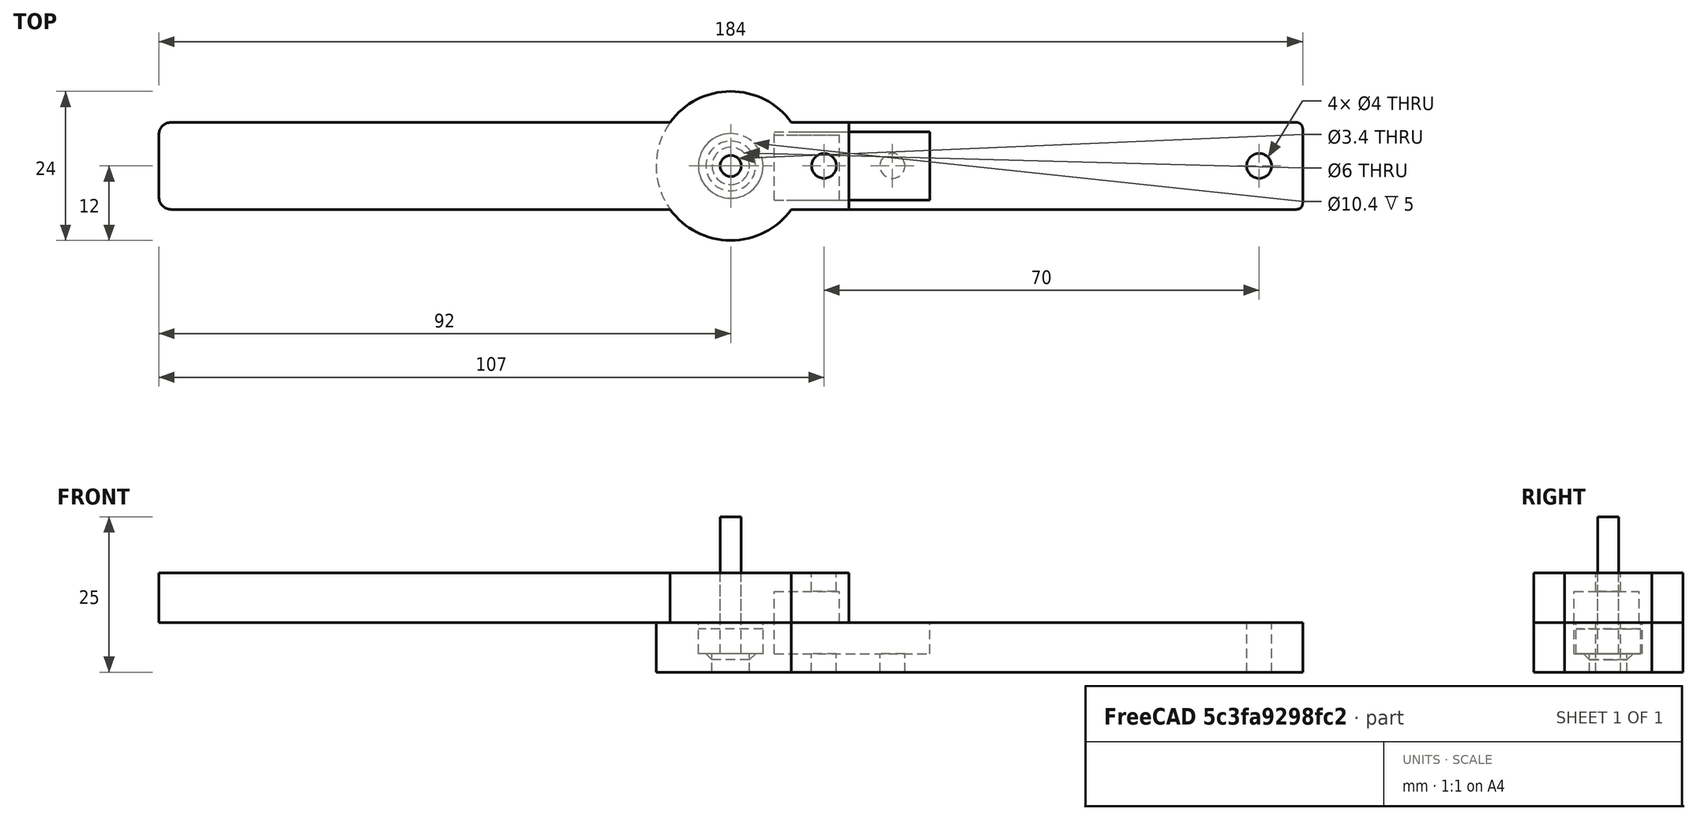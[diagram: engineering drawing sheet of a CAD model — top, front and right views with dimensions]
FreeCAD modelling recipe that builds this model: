
FCSTD DOCUMENT  (FreeCAD 0.17R13522 (Git))
Label: Magnet Testing parts
License: All rights reserved
LicenseURL: http://en.wikipedia.org/wiki/All_rights_reserved
objects: Part::Cylinder×14, Part::Cut×7, Part::Box×6, Part::Fuse×6, Part::Fillet×4, Part::Chamfer×1, Part::MultiFuse×1
note: 39 computed .brp shape members not serialized (recipe doc carries the construction recipe); baked Part::Feature solids carry a one-line shape summary decoded from their .brp

FEATURE [Part::Cylinder] Cylinder
  Angle = 360
  AttacherType = Attacher::AttachEngine3D
  Height = 8
  Radius = 12
FEATURE [Part::Box] Box  label="Long Magnet"
  AttacherType = Attacher::AttachEngine3D
  Height = 5
  Length = 25
  Placement = pos=(7,-5.5,3) rot=(0,0,1;0rad)
  Width = 11
FEATURE [Part::Cylinder] Cylinder001
  Angle = 360
  AttacherType = Attacher::AttachEngine3D
  Height = 25
  Radius = 1.7
FEATURE [Part::Cylinder] Cylinder002
  Angle = 360
  AttacherType = Attacher::AttachEngine3D
  Height = 3
  Radius = 3
FEATURE [Part::Cylinder] Cylinder003  label="bearing"
  Angle = 360
  AttacherType = Attacher::AttachEngine3D
  Height = 4
  Placement = pos=(0,0,3) rot=(0,0,1;0rad)
  Radius = 5.2
FEATURE [Part::Fuse] Fusion  label="Screw"
  Base = -> Cylinder001
  Tool = -> Cylinder002
FEATURE [Part::Cylinder] Cylinder004  label="bearing001"
  Angle = 360
  AttacherType = Attacher::AttachEngine3D
  Height = 5
  Placement = pos=(0,0,3) rot=(0,0,1;0rad)
  Radius = 5.2
FEATURE [Part::Cylinder] Cylinder005
  Angle = 360
  AttacherType = Attacher::AttachEngine3D
  Height = 25
  Radius = 1.7
FEATURE [Part::Cylinder] Cylinder006
  Angle = 360
  AttacherType = Attacher::AttachEngine3D
  Height = 3
  Radius = 3
FEATURE [Part::Fuse] Fusion001  label="Screw001"
  Base = -> Cylinder005
  Tool = -> Cylinder006
FEATURE [Part::Box] Box001  label="Cube"
  AttacherType = Attacher::AttachEngine3D
  Height = 8
  Length = 92
  Placement = pos=(0,-7,0) rot=(0,0,1;0rad)
  Width = 14
FEATURE [Part::Cylinder] Cylinder007  label="string hole"
  Angle = 360
  AttacherType = Attacher::AttachEngine3D
  Height = 10
  Placement = pos=(85,0,-1) rot=(0,0,1;0rad)
  Radius = 2
FEATURE [Part::Cylinder] Cylinder008  label="Cylinder007"
  Angle = 360
  AttacherType = Attacher::AttachEngine3D
  Height = 10
  Placement = pos=(15,0,-1) rot=(0,0,1;0rad)
  Radius = 2
FEATURE [Part::Cylinder] Cylinder009  label="Cylinder008"
  Angle = 360
  AttacherType = Attacher::AttachEngine3D
  Height = 10
  Placement = pos=(26,0,-1) rot=(0,0,1;0rad)
  Radius = 2
FEATURE [Part::Fuse] Fusion002
  Base = -> Cylinder
  Tool = -> Box001
FEATURE [Part::Box] Box002  label="Long Magnet001"
  AttacherType = Attacher::AttachEngine3D
  Height = 5
  Length = 25
  Placement = pos=(7,-5.5,3) rot=(0,0,1;0rad)
  Width = 11
FEATURE [Part::Cut] Cut
  Base = -> Fusion002
  Tool = -> Box002
FEATURE [Part::Fuse] Fusion003
  Base = -> Cylinder008
  Tool = -> Cylinder009
FEATURE [Part::Fuse] Fusion004
  Base = -> Cylinder004
  Tool = -> Fusion001
FEATURE [Part::Cut] Cut001
  Base = -> Cut
  Tool = -> Fusion003
FEATURE [Part::Cut] Cut002
  Base = -> Cut001
  Tool = -> Fusion004
FEATURE [Part::Cut] Cut003
  Base = -> Cut002
  Tool = -> Cylinder007
FEATURE [Part::Chamfer] Chamfer
  Base = -> Cut003
  Edges = 1 edges r=1: [Edge56]
FEATURE [Part::Fillet] Fillet
  Base = -> Chamfer
  Edges = 1 edges r=1: [Edge29]
FEATURE [Part::Fillet] Fillet001
  Base = -> Fillet
  Edges = 1 edges r=1: [Edge22]
FEATURE [Part::Cylinder] Cylinder010
  Angle = 360
  AttacherType = Attacher::AttachEngine3D
  Height = 8
  Placement = pos=(0,0,8) rot=(0,0,1;0rad)
  Radius = 12
FEATURE [Part::Box] Box003  label="Cube001"
  AttacherType = Attacher::AttachEngine3D
  Height = 8
  Length = 92
  Placement = pos=(-92,-7,8) rot=(0,0,1;0rad)
  Width = 14
FEATURE [Part::Cylinder] Cylinder011
  Angle = 360
  AttacherType = Attacher::AttachEngine3D
  Height = 25
  Radius = 1.7
FEATURE [Part::Cylinder] Cylinder012
  Angle = 360
  AttacherType = Attacher::AttachEngine3D
  Height = 3
  Radius = 3
FEATURE [Part::Fuse] Fusion005  label="Screw002"
  Base = -> Cylinder011
  Tool = -> Cylinder012
FEATURE [Part::Box] Box004  label="Square Magnet"
  AttacherType = Attacher::AttachEngine3D
  Height = 5
  Length = 10.5
  Placement = pos=(7,-5.5,8) rot=(0,0,1;0rad)
  Width = 10.5
FEATURE [Part::Box] Box005  label="Cube002"
  AttacherType = Attacher::AttachEngine3D
  Height = 8
  Length = 10
  Placement = pos=(9,-7,8) rot=(0,0,1;0rad)
  Width = 14
FEATURE [Part::Cylinder] Cylinder013
  Angle = 360
  AttacherType = Attacher::AttachEngine3D
  Height = 10
  Placement = pos=(15,0,8) rot=(0,0,1;0rad)
  Radius = 2
FEATURE [Part::MultiFuse] Fusion006
  Shapes = -> [Box005,Cylinder010,Box003]
FEATURE [Part::Cut] Cut004
  Base = -> Fusion006
  Tool = -> Fusion005
FEATURE [Part::Cut] Cut005
  Base = -> Cut004
  Tool = -> Box004
FEATURE [Part::Cut] Cut006
  Base = -> Cut005
  Tool = -> Cylinder013
FEATURE [Part::Fillet] Fillet002
  Base = -> Cut006
  Edges = 1 edges r=2: [Edge64]
FEATURE [Part::Fillet] Fillet003
  Base = -> Fillet002
  Edges = 1 edges r=2: [Edge22]
